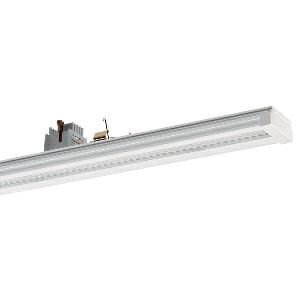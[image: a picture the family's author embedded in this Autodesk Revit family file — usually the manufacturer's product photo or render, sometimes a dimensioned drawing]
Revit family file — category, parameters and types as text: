
# Revit family: conveo_-_cvg_8000_850_xn-l_ea_5_226848469-00804985_fa04
name_source: partatom
category: Lighting Fixtures
units: mm (PartAtom-declared; Revit-internal decimal feet)

## family parameters
Cut with Voids When Loaded = No
Host = Face
Light Source = No
Part Type = Normal
Room Calculation Point = No
Round Connector Dimension = Use Diameter
Shared = No

## types (1)
- CONVEO - CVG 8000/850/xN-L/EA/5 (1 x LED, 8450 lm, 5000K)
    Apparent Load = 51 VA
    Approval mark = CE
    CIE Flux Codes = 84 95 99 100 100
    Color Rendering = 80-89
    Color Temperature = 5000K
    Control Gear = Electronic ballast
    Default Elevation = 1800 mm
    Description = CVG 8000/850/xN-L/EA/5|Continuous-row system|light source: LED|work equipment: Electronic ballast|connected load: 220-240 V, 50-60 Hz|Power consumption: approx. 51 W|luminous flux: 8450 lm|luminous efficacy: 165 lm/W|colour temperature: Cold white, ca. 5000 K|color rendering index (CRI): >= 80|chromaticity tolerance:  3 SDCM|System of protection: IP 54|class of protection: I|technology: Switchable|luminaire body|material: Aluminium|surface: Powder coatet|colour: White|lamp cover: Acrylic (PMMA), Satine|weight (net): approx. 1.9 kg|Fastening: Available separately|maximum ambient temperature: 46 ░C|glare control: Lens optics|Approval mark: VDE - ENEC|
    Frequency = 50 Hz
    Height = 70 mm
    Lamp = 1 x LED
    Lamp Light Flux = 8450 lm
    Lamp count = 1
    Length = 1500 mm
    Luminous efficacy = 166 lm/W
    Manufacturer = Waldmann
    ModVariant = No
    Model = 226848469-00804985
    Mounting Place = Ceiling
    Mounting Type = Pendant
    Number of Poles = 1
    OnlyDefault = Yes
    Power Factor = 1
    Product Name = CONVEO - CVG 8000/850/xN-L/EA/5
    Product group = Continuous-row system (industry)
    ProductGroupID = 301
    Protection Class = Protection class I
    Protection Degree = IP 54
    RLX_Detail_Level = 1
    RlxData = <blob elided: 100629 chars, md5=9413d3ad>
    Socket = socket
    Standby Power = 0 W
    System Light Flux = 8450 lm
    System Power = 51 W
    Type Comments = Product without accessories
    Type Image = 226848319-00804970_1l5.jpg
    URL = http://relux.com
    VarID = ---
    Voltage = 230 V
    Voltage Range = 220-240 V
    Weight = 0.00 kg
    Width = 64 mm

## geometry (parser evidence)
native form markers: Blend x4, Sweep x10
no freeform markers — native parametric forms only
